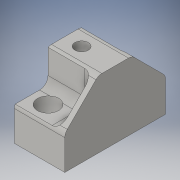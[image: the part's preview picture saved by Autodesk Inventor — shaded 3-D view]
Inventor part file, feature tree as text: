
AUTODESK INVENTOR PART (.ipt)
format: ipt  version: 2016 (Build 200138000, 138)  size: 201,216 bytes
history: native  units: in
note: dims shown in document units (in); Inventor stores cm internally (conversion verified against a paired STEP export)
features: extrude x6, sketch x6, projected_geometry x6, fillet x3
ambient origin geometry x8: Origin, YZ Plane, XZ Plane, XY Plane, X Axis, Y Axis, Z Axis, Center Point
bodies: Solid1 (feature_tree)
feature tree (21):
  extrude  "Extrusion1"  Depth=3.0in
  extrude  "Extrusion2"  Depth=1.0in
  extrude  "Extrusion3"  Depth=1.0in TaperAngle=0.0deg
  extrude  "Extrusion4"  Depth=3.5in TaperAngle=0.0deg
  extrude  "Extrusion5"  Depth=0.6299in
  extrude  "Extrusion6"  Depth=0.25in TaperAngle=0.0deg
  fillet  "Fillet1"  Radius=0.15in
  fillet  "Fillet2"  Radius=0.25in
  fillet  "Fillet3"  Radius=0.25in
  sketch  "Sketch1"  dims[d0=1.0in d1=3.0in]
  sketch  "Sketch2"  dims[d2=1.0in d3=0.0in d4=1.0in]
  projected_geometry  "Projected Loop1"
  sketch  "Sketch3"  dims[d5=1.0in d6=1.0in d7=0.0in]
  projected_geometry  "Projected Loop2"
  sketch  "Sketch4"  dims[d8=0.4in d9=3.5in d10=0.0in]
  projected_geometry  "Projected Loop3"
  projected_geometry  "Projected Loop4"
  sketch  "Sketch5"  dims[d11=0.6299in d12=0.6299in]
  projected_geometry  "Projected Loop5"
  sketch  "Sketch6"  dims[d13=3.5in d14=0.0in d15=0.5in d16=0.0in d17=0.15in d18=0.0in d19=0.25in d20=0.25in d21=0.25in]
  projected_geometry  "Projected Loop6"
